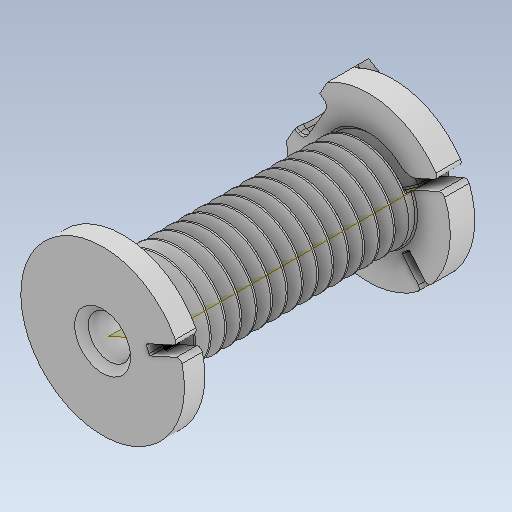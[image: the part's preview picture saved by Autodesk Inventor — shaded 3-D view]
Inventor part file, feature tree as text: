
AUTODESK INVENTOR PART (.ipt)
format: ipt  version: 2020 (Build 240168000, 168)  size: 1,135,104 bytes
history: native  units: mm
features: sketch x14, fillet x13, extrude x12, projected_geometry x12, other x4, thicken_offset x3, chamfer x2, plane x1, sweep x1, reference x1
ambient origin geometry x8: Origin, YZ Plane, XZ Plane, XY Plane, X Axis, Y Axis, Z Axis, Center Point
bodies: Solid1 (feature_tree)
feature tree (63):
  extrude  "Extrusion1"  Depth=12.0mm
  extrude  "Extrusion2"  Depth=3.0mm
  extrude  "Extrusion3"  Depth=18.0mm TaperAngle=0.0deg
  sketch  "3D Sketch1"
  plane  "Work Plane1"
  sweep  "Sweep1"
  extrude  "Extrusion4"  Depth=0.7mm
  extrude  "Extrusion5"  TaperAngle=0.0deg  [1 undecoded]
  fillet  "Fillet1"  Radius=5.0mm
  fillet  "Fillet2"  Radius=0.7mm
  fillet  "Fillet3"  Radius=1.0mm
  fillet  "Fillet4"  Radius=5.0mm
  fillet  "Fillet5"  Radius=0.7mm
  fillet  "Fillet6"  Radius=1.0mm
  extrude  "Extrusion6"  Depth=0.1mm
  thicken_offset  "Thicken1"
  thicken_offset  "Thicken2"
  extrude  "Extrusion7"  Depth=0.1mm
  extrude  "Extrusion8"  Depth=0.1mm
  extrude  "Extrusion9"  Depth=8.0mm
  chamfer  "Chamfer1"  Distance=2.0mm
  fillet  "Fillet7"  Radius=0.8mm
  fillet  "Fillet8"  Radius=0.8mm
  extrude  "Extrusion10"  Depth=0.5mm
  extrude  "Extrusion11"  Depth=0.4mm
  extrude  "Extrusion13"  Depth=0.4mm TaperAngle=0.0deg
  fillet  "Fillet10"  Radius=4.0mm
  fillet  "Fillet11"  Radius=0.8mm
  fillet  "Fillet12"  Radius=0.5mm
  fillet  "Fillet13"  Radius=0.5mm
  fillet  "Fillet14"  Radius=0.5mm
  thicken_offset  "Thicken3"
  chamfer  "Chamfer2"  Distance=3.490659mm
  sketch  "Sketch1"  dims[d0=3.0mm d1=12.0mm]
  reference  "Reference1"
  sketch  "Sketch2"  dims[d2=1.0mm d3=0.0mm d4=3.0mm]
  sketch  "Sketch3"  dims[d5=7.0mm d6=18.0mm d7=0.0mm]
  projected_geometry  "Projected Loop1"
  other  "Helical Curve2"
  sketch  "Sketch4"  dims[d8=1.0mm d9=0.0mm d14=18.0mm d15=160.0mm d16=7.0mm d17=0.0mm]
  projected_geometry  "Projected Loop2"
  projected_geometry  "Projected Loop3"
  sketch  "Sketch5"  dims[d18=0.5mm d19=0.7mm]
  projected_geometry  "Projected Loop4"
  sketch  "Sketch6"  dims[d20=0.5mm d21=0.0mm d22=0.0mm d23=5.0mm d24=0.7mm d25=1.0mm d26=0.0mm d27=5.0mm d28=0.7mm d29=1.0mm d30=0.0mm]
  projected_geometry  "Projected Loop5"
  sketch  "Sketch7"  dims[d31=1.0mm d32=0.1mm]
  projected_geometry  "Projected Loop6"
  sketch  "Sketch8"  dims[d33=0.1mm d34=0.1mm]
  projected_geometry  "Projected Loop7"
  sketch  "Sketch9"  dims[d35=1.0mm d36=0.1mm]
  projected_geometry  "Projected Loop8"
  sketch  "Sketch10"  dims[d37=30.0deg d38=8.0mm]
  projected_geometry  "Projected Loop9"
  sketch  "Sketch11"  dims[d39=6.0mm d40=2.0mm d41=0.0mm d42=0.8mm d43=0.8mm]
  projected_geometry  "Projected Loop10"
  sketch  "Sketch12"  dims[d44=0.5mm d45=0.5mm]
  projected_geometry  "Projected Loop11"
  sketch  "Sketch14"  dims[d46=4.0mm d47=0.0mm d48=1.4mm d49=4.0mm d50=0.0mm d51=4.0mm d52=0.8mm d53=0.0mm d54=0.5mm d55=2.0mm d56=45.0deg d57=0.5mm d58=0.5mm d59=3.490659mm d60=2.2mm d61=0.7mm d62=2.0mm d63=0.0mm d64=5.0mm d65=1.6mm d66=2.0mm d67=0.0mm d72=0.8mm d73=3.0mm d74=5.0mm d75=2.0mm d76=0.0mm d77=1.0mm d78=0.3mm d79=0.1mm d80=0.3mm d81=0.4mm d82=0.05mm d83=0.05mm d84=0.5mm d85=2.0mm d86=45.0deg]
  projected_geometry  "Projected Loop13"
  parser-record x1  (decoder bookkeeping rows leaked as tree rows — omitted from the tree; the rows remain in map.json)
  other  "tip2_ass_t1.iam"
  other  "bearing_3_6_2:1"
note: 1 required parameter value undecoded (feature->parameter linkage not recoverable at this tier; creation-order binding heuristic only, values carry confidence <= 0.55)
note: 1 file-system path scrubbed to <path> (originals preserved in map.json)
